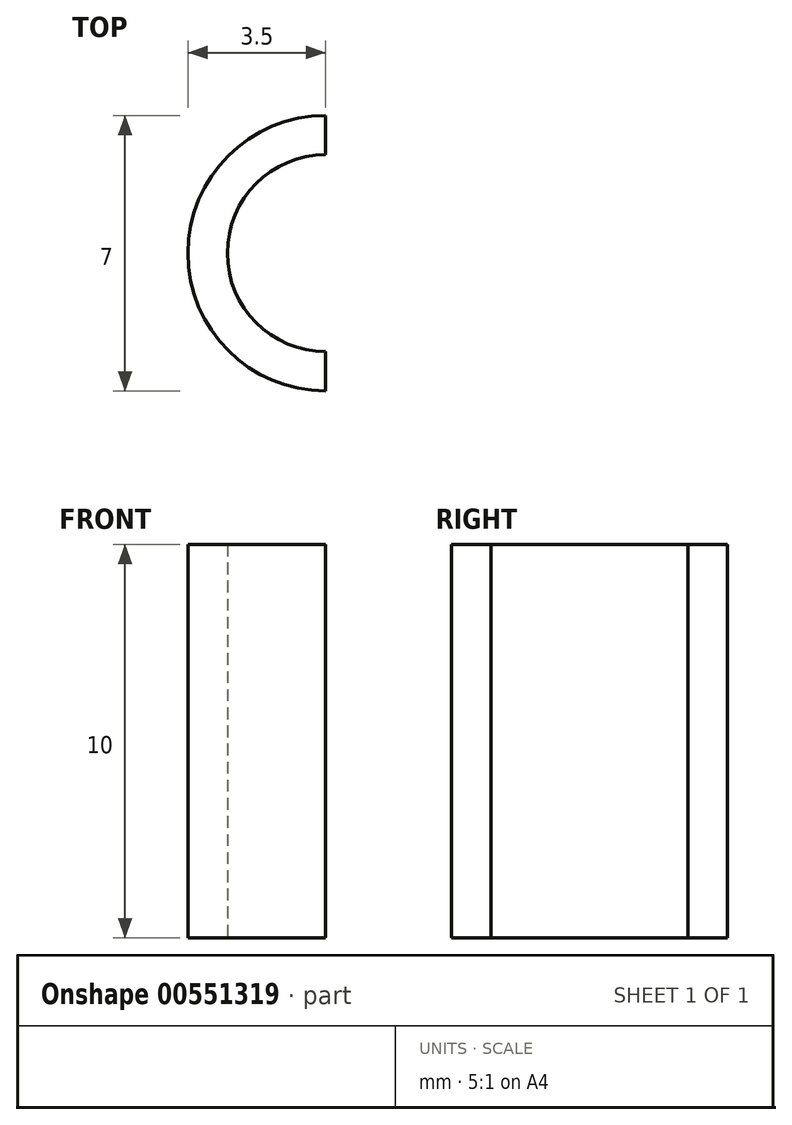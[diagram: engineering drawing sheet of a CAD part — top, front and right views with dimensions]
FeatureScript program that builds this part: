
annotation { "Feature Type Name" : "Feature", "Feature Type Description" : "" }
export const myFeature = defineFeature(function(context is Context, id is Id, definition is map)
    precondition{}
    {
        {
            var Q0;
            Q0=qCreatedBy(makeId("Top.planeOp"),FACE);
            var sketch = newSketch(context, id + "F0", { "sketchPlane" : qUnion([Q0])});
            skArc(sketch, "E0", {"start": v(0, -2.5) * mm, "mid": v(-2.5, 0) * mm, "end": v(0, 2.5) * mm});
            skArc(sketch, "E1.0", {"start": v(0, -3.5) * mm, "mid": v(-3.5, 0) * mm, "end": v(0, 3.5) * mm});
            skLineSegment(sketch, "E2", {"start": v(0, 3.5) * mm, "end": v(0, 2.5) * mm});
            skLineSegment(sketch, "E3", {"start": v(0, -2.5) * mm, "end": v(0, -3.5) * mm});
            skSolve(sketch);
        }
        {
            var Q0;
            Q0 = qSketchRegion(id + "F0", true);
            extrude(context, id + "F1", {"entities" : qUnion([Q0]), "depth" : 10 * mm, "offsetDistance" : 25 * mm});
        }
    });
